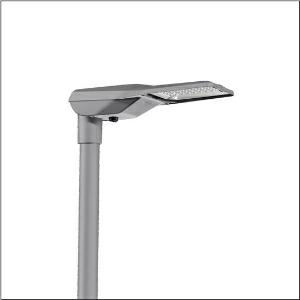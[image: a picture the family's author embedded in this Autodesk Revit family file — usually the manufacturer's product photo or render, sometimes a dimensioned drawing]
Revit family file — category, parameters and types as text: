
# Revit family: streetlight_sl_21_iq_mini___st1_0a_5xe2d31u08hb_e98e
name_source: partatom
category: Lighting Fixtures
units: mm (PartAtom-declared; Revit-internal decimal feet)

## family parameters
Cut with Voids When Loaded = No
Host = Face
Light Source = No
Part Type = Normal
Room Calculation Point = No
Round Connector Dimension = Use Diameter
Shared = No

## types (1)
- --- (1 x LED, 9750 lm, 71 W, 3000K)
    Apparent Load = 71 VA
    CIE Flux Codes = 37 72 97 100 100
    Color Rendering = 70
    Color Temperature = 3000K
    Default Elevation = 1800 mm
    Description = Streetlight SL 21 iQ mini, mast luminaire, primary light control with lens, of PMMA, primary optical cover: cover, of toughened safety glass, transparent, light distribution: ST1.0a, light emission: direct distribution, primary light characteristic: asymmetric, installation type: post-top, side-entry, LED, High Power LED, rated luminous flux: 9.750lm, luminous efficacy: 137lm/W, light colour: 730, colour temperature: 3000K, control: presetting dimming logarithmic, Street-Remote, Auto-Match, Temp-Guard, Lumen-Switch, Night-Set, Smart-Wire, Light-Fading, Desk-Remote (wireless, voltage-free reading and setting of iQ features in the workshop via application-optimized NFC function/RFID function), optimised constant luminous flux control (CLO 2.0), mains connection: 220..240V, AC, 50/60Hz, start of lifetime: 71W, end of service life: 75W, reduction: 30W, luminaire housing, of diecast aluminium, powder-coated, Siteco® metallic grey (DB 702S), corrosivity category C5 mid according to DIN EN ISO 12944, please order mast flange separately, inclination adjustable: 0°, 5°, 10°, 15°, sealing non-destructively replaceable, multi-level sealing system, length: 628mm, width: 235mm, height: 110mm, mast flange for spigot size: 42mm (side-entry): 5XC10008XM4, 60/48mm (side-entry/post-top): 5XC10108XM2, 76/60mm (side-entry/post-top): 5XC10108XM1, Smart Interface below, protection rating (complete): IP66, insulation class (complete): insulation class II (safety insulation), certification: CE, ENEC, ENEC+, VDE, impact resistance: IK09, permissible operating ambient temperature for outdoor applications: -40..+50°C, standard-compliant lighting for roads and squares, packaging unit: 1 piece

Light Distribution: ST1.0a
    Height = 110 mm
    Lamp = 1 x LED
    Lamp Light Flux = 9750 lm
    Lamp Power = 71 W
    Lamp count = 1
    Length = 625 mm
    Luminous efficacy = 137 lm/W
    Manufacturer = Siteco
    ModVariant = No
    Model = 5XE2D31U08HB
    Number of Poles = 1
    OnlyDefault = Yes
    Power Factor = 1
    Product Name = Streetlight SL 21 iQ mini | ST1.0a
    Product group = mast luminaire | pylon top
    ProductGroupID = 6100
    Protection Class = Protection class II
    Protection Degree = IP 66
    RLX_Detail_Level = 1
    RLX_Emergency_Light_Flux = 0 lm
    RLX_Emergency_Type = 0
    RLX_Emergency_Type_DB = No
    RlxData = <blob elided: 92545 chars, md5=48faa131>
    Socket = socket
    Standby Power = 0 W
    System Light Flux = 9750 lm
    System Power = 71 W
    Type Comments = factory setting: luminous flux: 100 % | dim-lin: 254 | 716 mA
    Type Image = l_1003516.jpg
    URL = http://relux.com
    VarID = @adj_063385
    Voltage = 0 V
    Weight = 0.00 kg
    Width = 234 mm

## geometry (parser evidence)
native form markers: Blend x4, Sweep x13
no freeform markers — native parametric forms only
